# Revit family: 98R031324
name_source: partatom
category: Furniture
units: mm (PartAtom-declared; Revit-internal decimal feet)

## family parameters
Always vertical = Yes
Cut with Voids When Loaded = No
Host = Wall
Room Calculation Point = No
Shared = No

## types (1)
- 98R031324
    36W CL = No
    Cover ADJ = 0' - 6"
    Depth = 0' - 11 1/2"
    Description = Partially Recessed 13.5' double depth, 2" side flange
    Double Retro-Fit = Yes
    Edge Ext-Dist = 0' - 0 7/16"
    H-CL-10"L-1 = Yes
    Manufacturer = Palmer Hamilton
    Model = 98R031324
    Product = https://palmerhamilton.com
    Side Ch = 0' - 5 1/2"
    T-Edge-Dist = 0' - 0 1/2"
    Top Frame B-H = 0' - 4 23/32"
    Top Frame D = 0' - 6 1/16"
    Top Frame F-H = 0' - 2 5/16"
    Type Comments = Wall Pocket
    URL = https://palmerhamilton.com
    V-4.5-1 = No
    V-CL-1 = Yes
    V-CL-2 = No
    V-CL-5 = Yes
    V-CL-7 = No

## geometry (parser evidence)
native form markers: Sweep x14
no freeform markers — native parametric forms only
